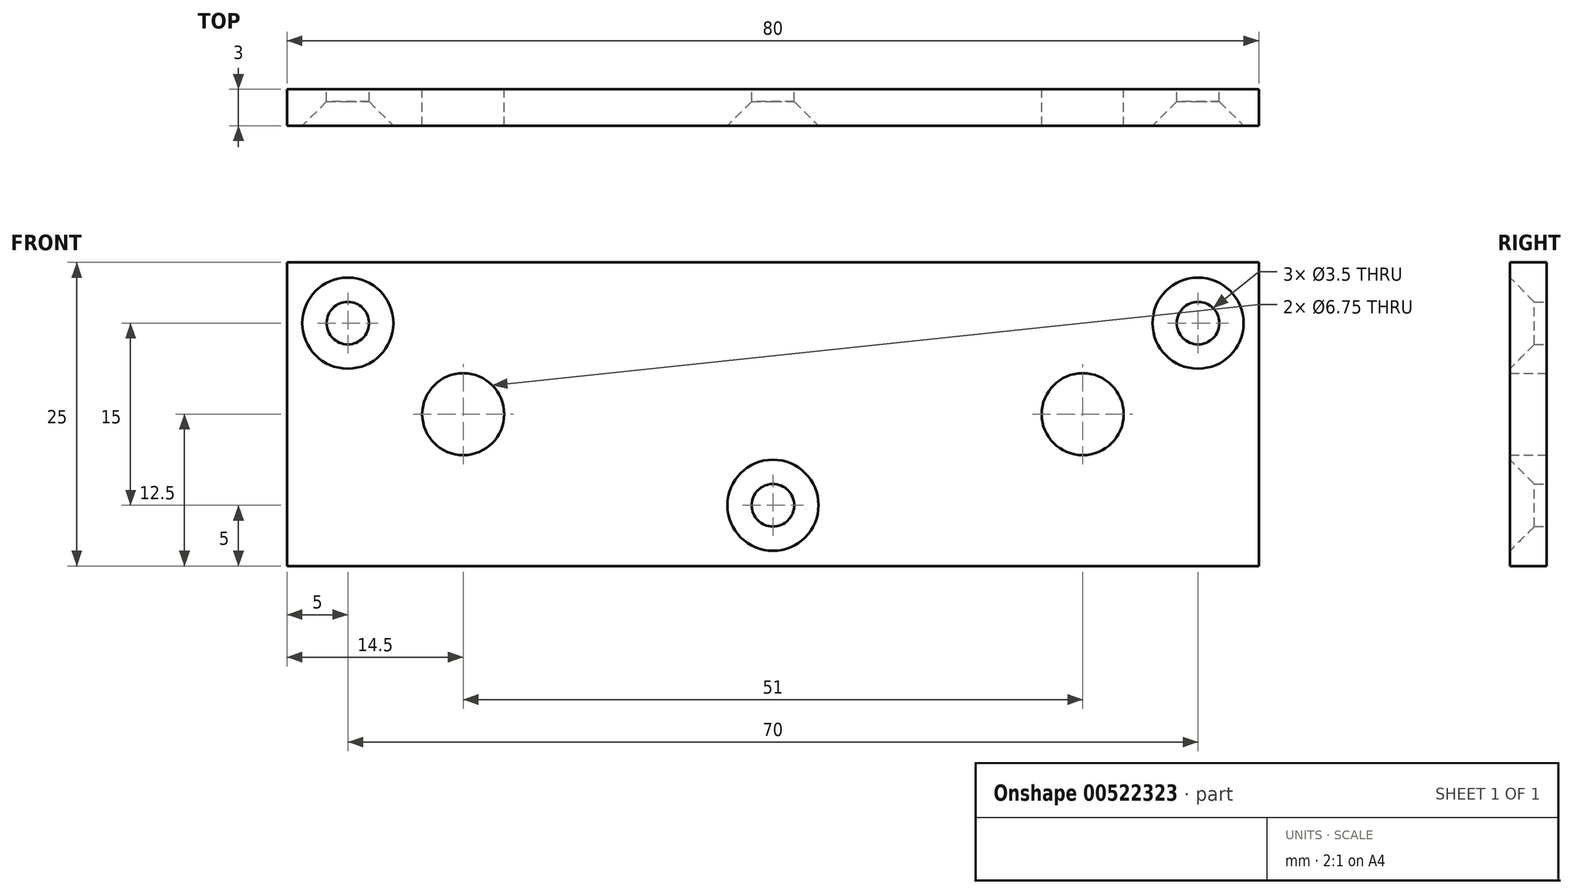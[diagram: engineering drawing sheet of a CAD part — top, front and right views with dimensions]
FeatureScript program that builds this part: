
annotation { "Feature Type Name" : "Feature", "Feature Type Description" : "" }
export const myFeature = defineFeature(function(context is Context, id is Id, definition is map)
    precondition{}
    {
        {
            var Q0;
            Q0=qCreatedBy(makeId("Front.planeOp"),FACE);
            var sketch = newSketch(context, id + "F0", { "sketchPlane" : qUnion([Q0])});
            skLineSegment(sketch, "E0.bottom", {"start": v(40, 12.5) * mm, "end": v(-40, 12.5) * mm});
            skLineSegment(sketch, "E0.top", {"start": v(40, -12.5) * mm, "end": v(-40, -12.5) * mm});
            skLineSegment(sketch, "E0.left", {"start": v(40, 12.5) * mm, "end": v(40, -12.5) * mm});
            skLineSegment(sketch, "E0.right", {"start": v(-40, 12.5) * mm, "end": v(-40, -12.5) * mm});
            skPoint(sketch, "E0.middle", {"position": v(0, 0) * mm});
            skCircle(sketch, "E1", {"center": v(-25.5, 0) * mm, "radius": 3.38 * mm});
            skCircle(sketch, "E2", {"center": v(25.5, 0) * mm, "radius": 3.38 * mm});
            skLineSegment(sketch, "E3", {"start": v(-25.5, 0) * mm, "end": v(25.5, 0) * mm, "construction": true});
            skCircle(sketch, "E4.cCircle", {"center": v(-25.5, 0) * mm, "radius": 6.5 * mm, "construction": true});
            skLineSegment(sketch, "E4.0", {"start": v(-19, 3.75) * mm, "end": v(-19, -3.75) * mm, "construction": true});
            skLineSegment(sketch, "E4.1", {"start": v(-19, -3.75) * mm, "end": v(-25.5, -7.5) * mm, "construction": true});
            skLineSegment(sketch, "E4.2", {"start": v(-25.5, -7.5) * mm, "end": v(-32, -3.75) * mm, "construction": true});
            skLineSegment(sketch, "E4.3", {"start": v(-32, -3.75) * mm, "end": v(-32, 3.75) * mm, "construction": true});
            skLineSegment(sketch, "E4.4", {"start": v(-32, 3.75) * mm, "end": v(-25.5, 7.5) * mm, "construction": true});
            skLineSegment(sketch, "E4.5", {"start": v(-25.5, 7.5) * mm, "end": v(-19, 3.75) * mm, "construction": true});
            skPoint(sketch, "E4.0.midPoint", {"position": v(-19, 0) * mm});
            skCircle(sketch, "E5.cCircle", {"center": v(25.5, 0) * mm, "radius": 6.5 * mm, "construction": true});
            skLineSegment(sketch, "E5.0", {"start": v(19, 3.75) * mm, "end": v(25.5, 7.5) * mm, "construction": true});
            skLineSegment(sketch, "E5.1", {"start": v(25.5, 7.5) * mm, "end": v(32, 3.75) * mm, "construction": true});
            skLineSegment(sketch, "E5.2", {"start": v(32, 3.75) * mm, "end": v(32, -3.75) * mm, "construction": true});
            skLineSegment(sketch, "E5.3", {"start": v(32, -3.75) * mm, "end": v(25.5, -7.5) * mm, "construction": true});
            skLineSegment(sketch, "E5.4", {"start": v(25.5, -7.5) * mm, "end": v(19, -3.75) * mm, "construction": true});
            skLineSegment(sketch, "E5.5", {"start": v(19, -3.75) * mm, "end": v(19, 3.75) * mm, "construction": true});
            skPoint(sketch, "E5.0.midPoint", {"position": v(22.25, 5.63) * mm});
            skCircle(sketch, "E6", {"center": v(0, -7.5) * mm, "radius": 1.75 * mm});
            skCircle(sketch, "E7", {"center": v(35, 7.5) * mm, "radius": 1.75 * mm});
            skCircle(sketch, "E8", {"center": v(-35, 7.5) * mm, "radius": 1.75 * mm});
            skCircle(sketch, "E9", {"center": v(-35, 7.5) * mm, "radius": 3.5 * mm, "construction": true});
            skCircle(sketch, "E10", {"center": v(35, 7.5) * mm, "radius": 3.5 * mm, "construction": true});
            skCircle(sketch, "E11", {"center": v(0, -7.5) * mm, "radius": 3.5 * mm, "construction": true});
            skSolve(sketch);
        }
        {
            var Q0;
            Q0 = qSketchRegion(id + "F0", true);
            extrude(context, id + "F1", {"entities" : qUnion([Q0]), "depth" : 3 * mm, "offsetDistance" : 25 * mm});
        }
        {
            var Q0;
            Q0=makeQuery(id+"F1.opExtrude","CAP_EDGE",EDGE,{"disambiguationData":[OSD([sQuery(id+"F0.wireOp",EDGE,"E8")])],"isStart":false});
            var Q1;
            Q1=makeQuery(id+"F1.opExtrude","CAP_EDGE",EDGE,{"disambiguationData":[OSD([sQuery(id+"F0.wireOp",EDGE,"E6")])],"isStart":false});
            var Q2;
            Q2=makeQuery(id+"F1.opExtrude","CAP_EDGE",EDGE,{"disambiguationData":[OSD([sQuery(id+"F0.wireOp",EDGE,"E7")])],"isStart":false});
            chamfer(context, id + "F2", {"entities" : qUnion([Q0, Q1, Q2]), "width" : 2 * mm, "tangentPropagation" : true});
        }
    });
